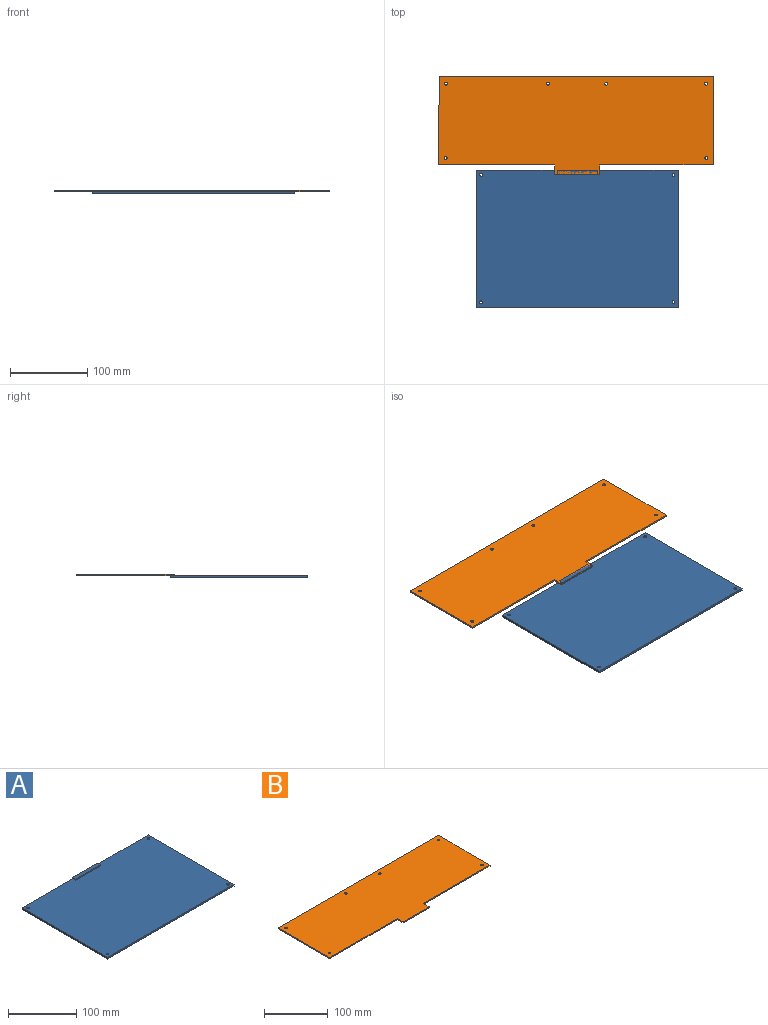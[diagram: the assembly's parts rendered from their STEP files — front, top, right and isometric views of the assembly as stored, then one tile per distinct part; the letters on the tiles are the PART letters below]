
ASSEMBLY  parts=2 mates=1
PART A: 14 faces, bbox 262.1x177.8x5 mm
  f0: plane 262.13x177.8mm, normal (0,0,1), area 46248mm2, adj f1,f2,f3,f4,f5,f6,f7,f8
  f1: plane 262.13x5mm, normal (0,1,0), area 890.6mm2, adj f0,f2,f7,f9,f10,f12,f13
  f2: plane 177.8x3mm, normal (-1,0,0), area 533.4mm2, adj f0,f1,f3,f9
  f3: plane 262.13x3mm, normal (0,-1,0), area 786.4mm2, adj f0,f2,f7,f9
  f4: cylinder r=1.91mm len=3.81mm, axis (0,0,-1), area 35.9mm2, adj f0,f9
  f5: cylinder r=1.91mm len=3.81mm, axis (0,0,-1), area 35.9mm2, adj f0,f9
  f6: cylinder r=1.91mm len=3.81mm, axis (0,0,-1), area 35.9mm2, adj f0,f9
  f7: plane 177.8x3mm, normal (1,0,0), area 533.4mm2, adj f0,f1,f3,f9
  f8: cylinder r=1.91mm len=3.81mm, axis (0,0,-1), area 35.9mm2, adj f0,f9
  f9: plane 262.13x177.8mm, normal (0,0,-1), area 46560.8mm2, adj f1,f2,f3,f4,f5,f6,f7,f8
  f10: plane 6x2mm, normal (-1,0,0), area 12mm2, adj f0,f1,f11,f13
  f11: plane 52.13x2mm, normal (0,-1,0), area 104.3mm2, adj f0,f10,f12,f13
  f12: plane 6x2mm, normal (1,0,0), area 12mm2, adj f0,f1,f11,f13
  f13: plane 52.13x6mm, normal (0,0,1), area 312.8mm2, adj f1,f10,f11,f12
PART B: 16 faces, bbox 355.9x127x2 mm
  f0: plane 355.6x2mm, normal (0,1,0), area 711.2mm2, adj f1,f12,f14,f15
  f1: plane 114.3x2mm, normal (-1,0,0), area 228.6mm2, adj f0,f2,f14,f15
  f2: plane 150.62x2mm, normal (0,-1,0), area 301.2mm2, adj f1,f3,f14,f15
  f3: plane 12.7x2mm, normal (-1,0,0), area 25.4mm2, adj f2,f4,f14,f15
  f4: plane 57.93x2mm, normal (0,-1,0), area 115.9mm2, adj f3,f5,f14,f15
  f5: plane 12.7x2mm, normal (1,0,0), area 25.4mm2, adj f4,f6,f14,f15
  f6: plane 147.32x2mm, normal (0,-1,0), area 294.6mm2, adj f5,f12,f14,f15
  f7: cylinder r=1.91mm len=3.81mm, axis (0,0,-1), area 23.9mm2, adj f14,f15
  f8: cylinder r=1.91mm len=3.81mm, axis (0,0,-1), area 23.9mm2, adj f14,f15
  f9: cylinder r=1.91mm len=3.81mm, axis (0,0,-1), area 23.9mm2, adj f14,f15
  f10: cylinder r=1.91mm len=3.81mm, axis (0,0,-1), area 23.9mm2, adj f14,f15
  f11: cylinder r=1.91mm len=3.81mm, axis (0,0,-1), area 23.9mm2, adj f14,f15
  f12: plane 114.3x2mm, normal (1,0,0), area 228.6mm2, adj f0,f6,f14,f15
  f13: cylinder r=1.91mm len=3.81mm, axis (0,0,-1), area 23.9mm2, adj f14,f15
  f14: plane 355.87x127mm, normal (0,0,1), area 41327.7mm2, adj f0,f1,f2,f3,f4,f5,f6,f7
  f15: plane 355.87x127mm, normal (0,0,-1), area 41327.7mm2, adj f0,f1,f2,f3,f4,f5,f6,f7
PLACE A t=(-23.83,-17.9,22.14)mm
PLACE B t=(-23.16,-111.15,-4.86)mm
MATE planar B.f4 <-> A.f11  axis (0,-1,0) through (94.53,153.9,26.14)mm
